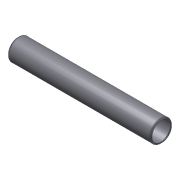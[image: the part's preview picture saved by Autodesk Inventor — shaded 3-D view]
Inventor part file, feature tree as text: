
AUTODESK INVENTOR PART (.ipt)
format: ipt  version: 2012 (Build 160160000, 160)  size: 114,176 bytes
history: native  units: mm (DEFAULTED — no unit token found)
features: other x42, revolve x1, sketch x1
ambient origin geometry x8: Origin, YZ Plane, XZ Plane, XY Plane, X Axis, Y Axis, Z Axis, Center Point
bodies: Solid1 (feature_tree)
feature tree (44):
  revolve  "Revolution1"  [1 undecoded]
  other  "tube_front_XY"
  other  "tube_front_YZ"
  other  "tube_front_ZX"
  other  "tube_front_X"
  other  "tube_front_Y"
  other  "tube_front_Z"
  other  "tube_front_Center"
  other  "tube_rear_XY"
  other  "tube_rear_YZ"
  other  "tube_rear_ZX"
  other  "tube_rear_X"
  other  "tube_rear_Y"
  other  "tube_rear_Z"
  other  "tube_rear_Center"
  other  "cp1_XY"
  other  "cp1_YZ"
  other  "cp1_ZX"
  other  "cp1_X"
  other  "cp1_Y"
  other  "cp1_Z"
  other  "cp1_Center"
  other  "cp2_XY"
  other  "cp2_YZ"
  other  "cp2_ZX"
  other  "cp2_X"
  other  "cp2_Y"
  other  "cp2_Z"
  other  "cp2_Center"
  other  "cp3_XY"
  other  "cp3_YZ"
  other  "cp3_ZX"
  other  "cp3_X"
  other  "cp3_Y"
  other  "cp3_Z"
  other  "cp3_Center"
  other  "cp4_XY"
  other  "cp4_YZ"
  other  "cp4_ZX"
  other  "cp4_X"
  other  "cp4_Y"
  other  "cp4_Z"
  other  "cp4_Center"
  sketch  "Sketch_1"  dims[d0=360.0deg]
note: 1 required parameter value undecoded (feature->parameter linkage not recoverable at this tier; creation-order binding heuristic only, values carry confidence <= 0.55)
